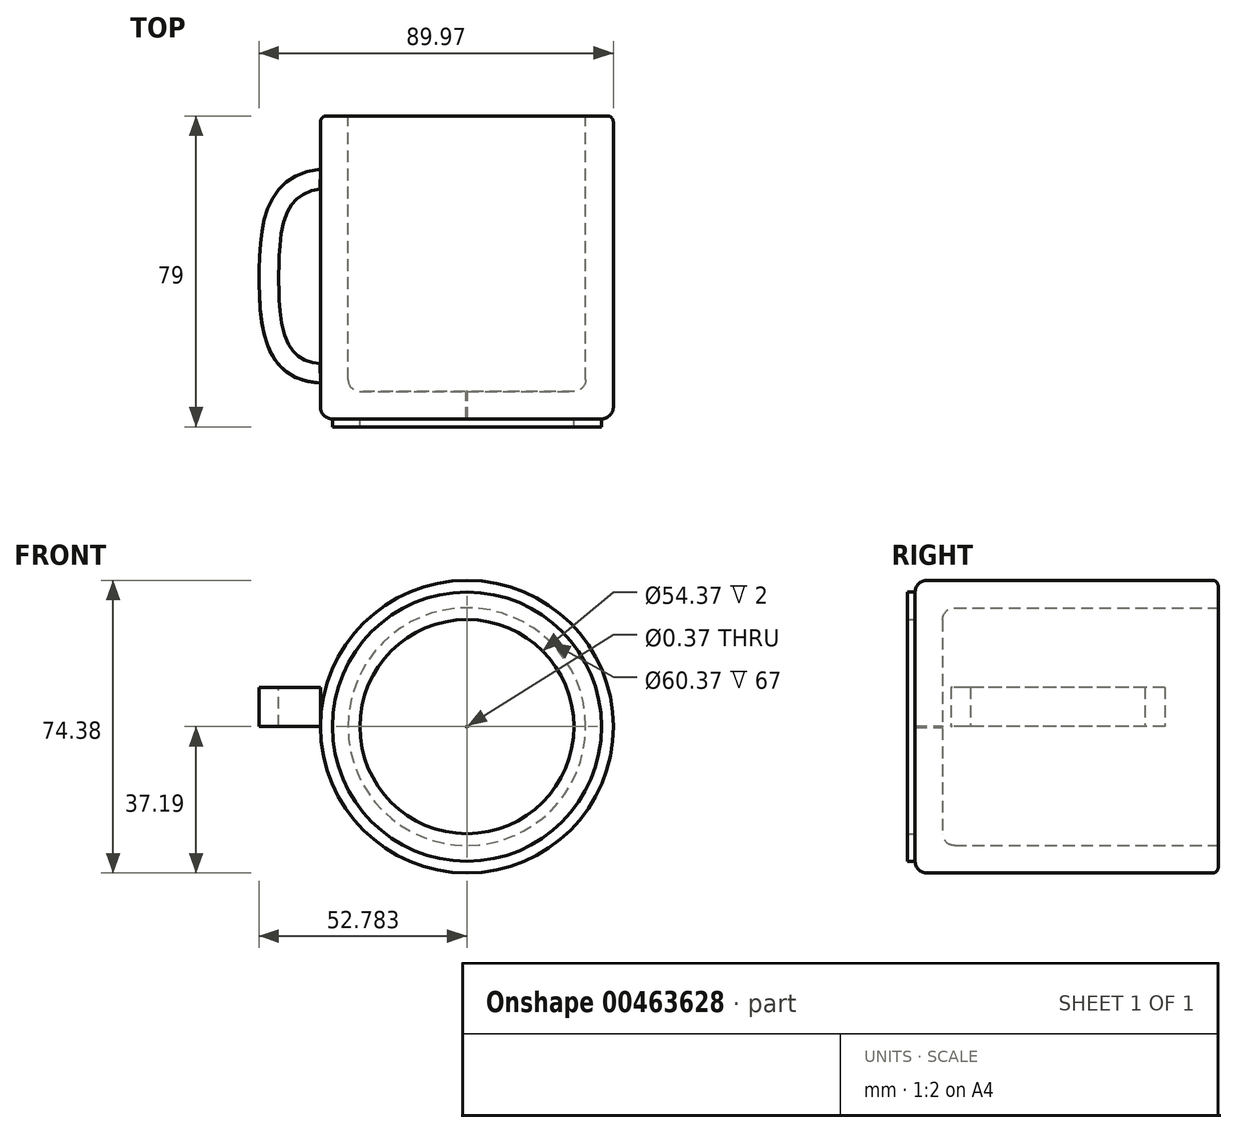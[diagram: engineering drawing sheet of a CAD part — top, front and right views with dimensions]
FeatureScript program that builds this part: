
annotation { "Feature Type Name" : "Feature", "Feature Type Description" : "" }
export const myFeature = defineFeature(function(context is Context, id is Id, definition is map)
    precondition{}
    {
        {
            var Q0;
            Q0=qCreatedBy(makeId("Top.planeOp"),FACE);
            var sketch = newSketch(context, id + "F0", { "sketchPlane" : qUnion([Q0])});
            skLineSegment(sketch, "E0", {"start": v(-32.25, 39.35) * mm, "end": v(-32.25, -33.15) * mm});
            skLineSegment(sketch, "E1", {"start": v(-30.75, 40.85) * mm, "end": v(-25.25, 40.85) * mm});
            skPoint(sketch, "E2.visualSharp", {"position": v(-32.25, 40.85) * mm});
            skArc(sketch, "E2.filletArc", {"start": v(-30.75, 40.85) * mm, "mid": v(-31.81, 40.41) * mm, "end": v(-32.25, 39.35) * mm});
            skLineSegment(sketch, "E3", {"start": v(-25.25, 40.85) * mm, "end": v(-25.25, -26.15) * mm});
            skLineSegment(sketch, "E4", {"start": v(-22.25, -29.15) * mm, "end": v(4.75, -29.15) * mm});
            skLineSegment(sketch, "E5", {"start": v(4.75, -29.15) * mm, "end": v(4.75, -36.15) * mm});
            skLineSegment(sketch, "E6", {"start": v(4.75, -36.15) * mm, "end": v(-22.25, -36.15) * mm});
            skLineSegment(sketch, "E7", {"start": v(-22.25, -36.15) * mm, "end": v(-22.25, -38.15) * mm});
            skLineSegment(sketch, "E8", {"start": v(-22.25, -38.15) * mm, "end": v(-29.25, -38.15) * mm});
            skLineSegment(sketch, "E9", {"start": v(-29.25, -38.15) * mm, "end": v(-29.25, -36.15) * mm});
            skLineSegment(sketch, "E10", {"start": v(-29.25, -36.15) * mm, "end": v(-29.25, -36.15) * mm});
            skPoint(sketch, "E11.visualSharp", {"position": v(-25.25, -29.15) * mm});
            skArc(sketch, "E11.filletArc", {"start": v(-25.25, -26.15) * mm, "mid": v(-24.37, -28.27) * mm, "end": v(-22.25, -29.15) * mm});
            skPoint(sketch, "E12.visualSharp", {"position": v(-32.25, -36.15) * mm});
            skArc(sketch, "E12.filletArc", {"start": v(-32.25, -33.15) * mm, "mid": v(-31.37, -35.27) * mm, "end": v(-29.25, -36.15) * mm});
            skPoint(sketch, "E13.startSnap0", {"position": v(4.75, -32.65) * mm});
            skSolve(sketch);
        }
        {
            var Q0;
            Q0=qCreatedBy(makeId("Top.planeOp"),FACE);
            var sketch = newSketch(context, id + "F1", { "sketchPlane" : qUnion([Q0])});
            skLineSegment(sketch, "E14", {"start": v(4.93, -9.16) * mm, "end": v(4.93, -53.04) * mm});
            skSolve(sketch);
        }
        {
            var Q0;
            Q0=makeQuery(id+"F0.imprint","IMPRINT",FACE,{"disambiguationData":[TD([[makeQuery(id+"F0.imprint","IMPRINT",EDGE,{"derivedFrom":sQuery(id+"F0.wireOp",EDGE,"E0")}),1.0]])]});
            var Q1;
            Q1=sQuery(id+"F1.wireOp",EDGE,"E14");
            revolve(context, id + "F2", {"entities" : qUnion([Q0]), "axis" : qUnion([Q1]), "revolveType" : RevolveType.FULL});
        }
        {
            var Q0;
            Q0=qCreatedBy(makeId("Top.planeOp"),FACE);
            var sketch = newSketch(context, id + "F3", { "sketchPlane" : qUnion([Q0])});
            skFitSpline(sketch, "E15", {"points": [v(-32.27, 27.32) * mm, v(-47.85, 0) * mm, v(-32.25, -27.07) * mm], "startDerivative": vector(-85.87, -9.81) * mm, "endDerivative": vector(86.34, -4.93) * mm});
            skFitSpline(sketch, "E16.0", {"points": [v(-31.7, 22.35) * mm, v(-33.13, 22.18) * mm, v(-34.9, 21.75) * mm, v(-36.65, 20.94) * mm, v(-37.74, 20.23) * mm, v(-38.67, 19.41) * mm, v(-39.48, 18.46) * mm, v(-40.2, 17.34) * mm, v(-41.04, 15.6) * mm, v(-41.88, 12.94) * mm, v(-42.4, 9.73) * mm, v(-42.66, 6.92) * mm, v(-42.78, 4.71) * mm, v(-42.83, 2.8) * mm, v(-42.85, 1.25) * mm, v(-42.85, 0.06) * mm, v(-42.85, -1.12) * mm, v(-42.83, -2.69) * mm, v(-42.79, -4.62) * mm, v(-42.67, -6.86) * mm, v(-42.42, -9.73) * mm, v(-41.9, -13.02) * mm, v(-41.06, -15.74) * mm, v(-40.21, -17.5) * mm, v(-39.5, -18.6) * mm, v(-38.71, -19.53) * mm, v(-37.83, -20.3) * mm, v(-36.8, -20.94) * mm, v(-35.53, -21.47) * mm, v(-33.96, -21.88) * mm, v(-32.67, -22.03) * mm, v(-31.97, -22.07) * mm]});
            skLineSegment(sketch, "E17", {"start": v(-32.27, 27.32) * mm, "end": v(-32.31, 22.27) * mm});
            skLineSegment(sketch, "E18", {"start": v(-32.33, -22.05) * mm, "end": v(-32.25, -27.07) * mm});
            skSolve(sketch);
        }
        {
            var Q0;
            Q0=makeQuery(id+"F3.imprint","IMPRINT",FACE,{"disambiguationData":[TD([[makeQuery(id+"F3.imprint","IMPRINT",EDGE,{"derivedFrom":sQuery(id+"F3.wireOp",EDGE,"E15")}),1.0]])]});
            extrude(context, id + "F4", {"entities" : qUnion([Q0]), "operationType" : NewBodyOperationType.ADD, "depth" : 10 * mm});
        }
    });
